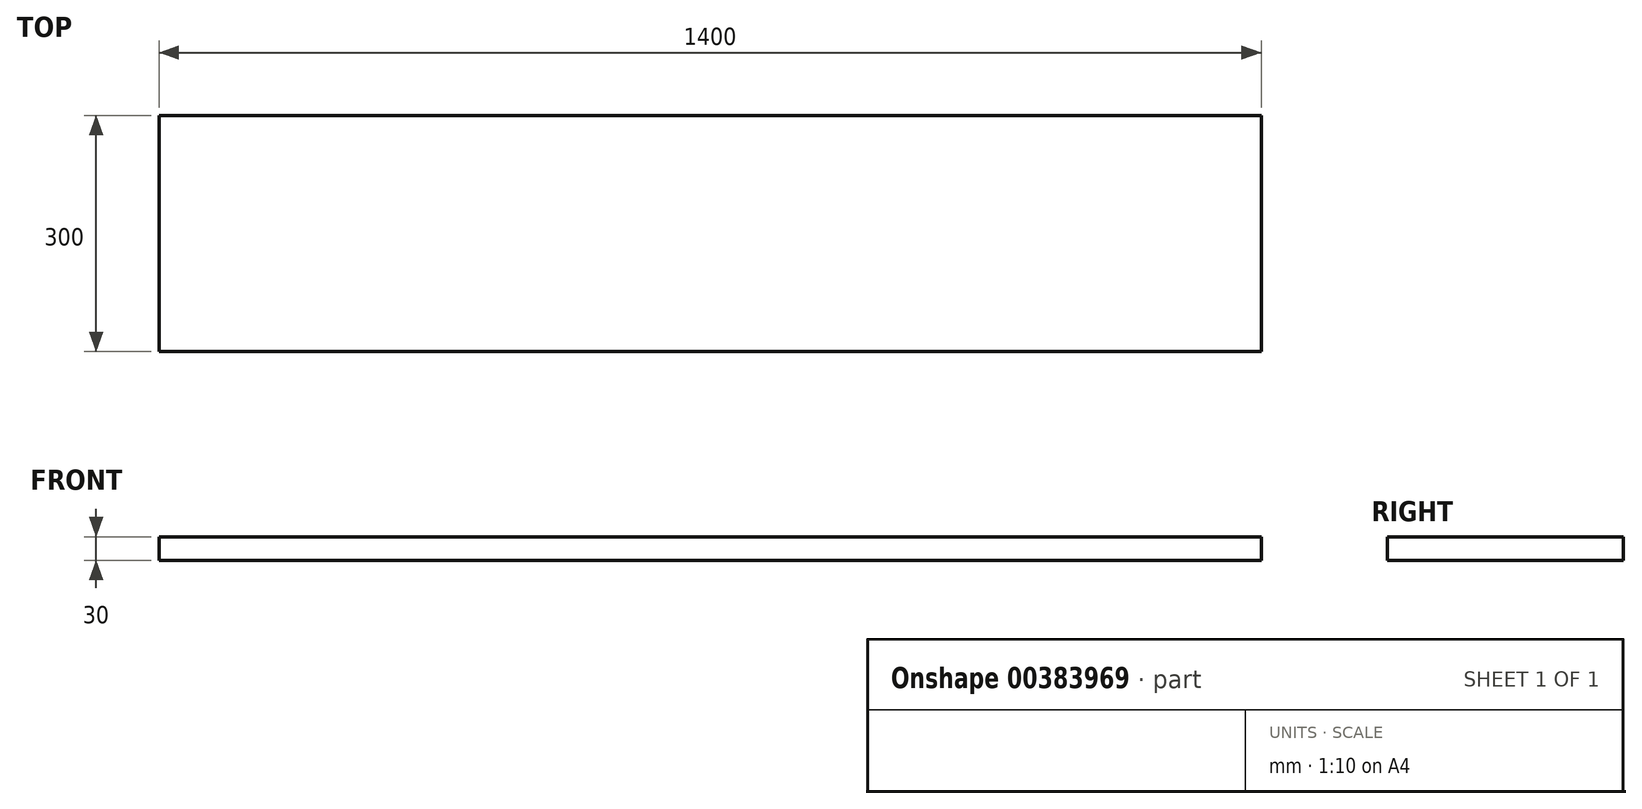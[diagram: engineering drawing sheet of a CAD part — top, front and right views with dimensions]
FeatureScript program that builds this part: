
annotation { "Feature Type Name" : "Feature", "Feature Type Description" : "" }
export const myFeature = defineFeature(function(context is Context, id is Id, definition is map)
    precondition{}
    {
        {
            var Q0;
            Q0=qCreatedBy(makeId("Top.planeOp"),FACE);
            var sketch = newSketch(context, id + "F0", { "sketchPlane" : qUnion([Q0])});
            skLineSegment(sketch, "E0.bottom", {"start": v(-700, 150) * mm, "end": v(700, 150) * mm});
            skLineSegment(sketch, "E0.top", {"start": v(-700, -150) * mm, "end": v(700, -150) * mm});
            skLineSegment(sketch, "E0.left", {"start": v(-700, 150) * mm, "end": v(-700, -150) * mm});
            skLineSegment(sketch, "E0.right", {"start": v(700, 150) * mm, "end": v(700, -150) * mm});
            skPoint(sketch, "E0.middle", {"position": v(0, 0) * mm});
            skSolve(sketch);
        }
        {
            var Q0;
            Q0=qSketchRegion(id+"F0",true);
            extrude(context, id + "F1", {"entities" : qUnion([Q0]), "endBound" : BoundingType.SYMMETRIC, "depth" : 30 * mm});
        }
    });
